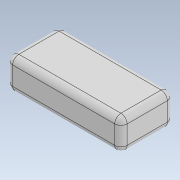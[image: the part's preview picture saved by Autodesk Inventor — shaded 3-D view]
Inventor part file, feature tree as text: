
AUTODESK INVENTOR PART (.ipt)
format: ipt  version: 2020.2 (Build 242310000, 310)  size: 108,544 bytes
history: native  units: in
note: dims shown in document units (in); Inventor stores cm internally (conversion verified against a paired STEP export)
features: extrude x1, fillet x1, sketch x1
ambient origin geometry x8: Origin, YZ Plane, XZ Plane, XY Plane, X Axis, Y Axis, Z Axis, Center Point
bodies: Solid1 (feature_tree)
feature tree (3):
  extrude  "Extrusion1"  Depth=0.7874in
  fillet  "Fillet1"  Radius=1.3386in
  sketch  "Sketch1"  dims[d0=2.9134in d1=0.7874in d2=1.3386in d3=0.0in d4=0.1575in]
